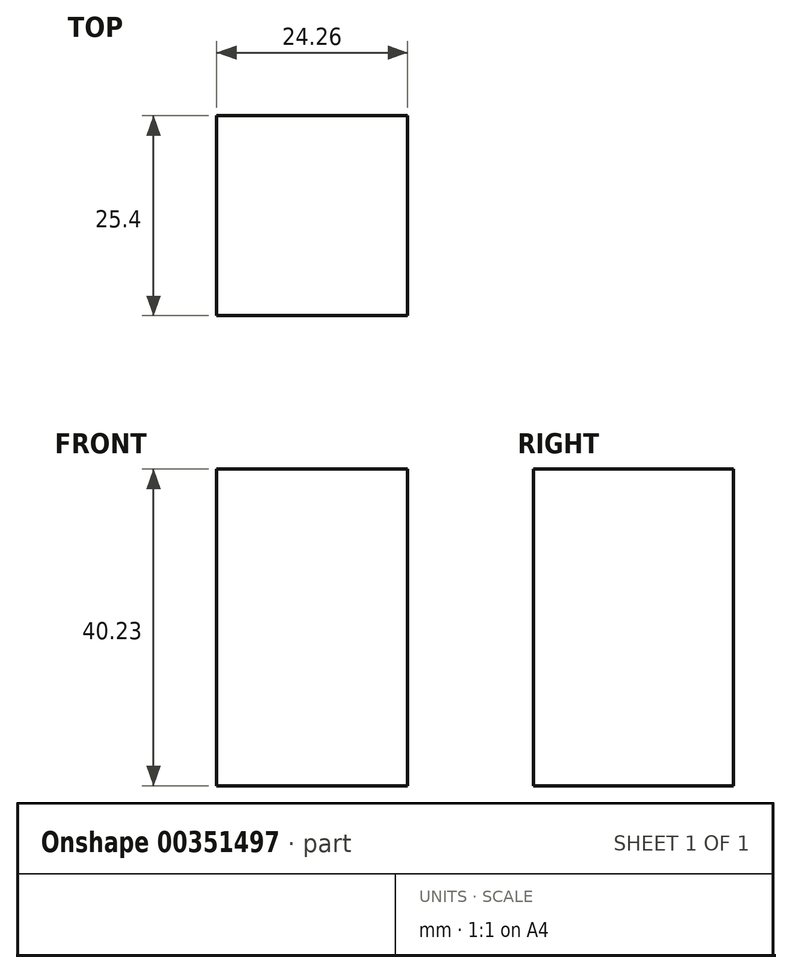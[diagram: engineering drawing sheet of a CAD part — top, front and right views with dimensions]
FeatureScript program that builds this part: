
annotation { "Feature Type Name" : "Feature", "Feature Type Description" : "" }
export const myFeature = defineFeature(function(context is Context, id is Id, definition is map)
    precondition{}
    {
        {
            var Q0;
            Q0=qCreatedBy(makeId("Front.planeOp"),FACE);
            var sketch = newSketch(context, id + "F0", { "sketchPlane" : qUnion([Q0])});
            skLineSegment(sketch, "E0.bottom", {"start": v(0, 0) * mm, "end": v(24.26, 0) * mm});
            skLineSegment(sketch, "E0.top", {"start": v(0, 40.23) * mm, "end": v(24.26, 40.23) * mm});
            skLineSegment(sketch, "E0.left", {"start": v(0, 0) * mm, "end": v(0, 40.23) * mm});
            skLineSegment(sketch, "E0.right", {"start": v(24.26, 0) * mm, "end": v(24.26, 40.23) * mm});
            skSolve(sketch);
        }
        {
            var Q0;
            Q0=makeQuery(id+"F0.imprint","IMPRINT",FACE,{"disambiguationData":[TD([[makeQuery(id+"F0.imprint","IMPRINT",EDGE,{"derivedFrom":sQuery(id+"F0.wireOp",EDGE,"E0.bottom")}),1.0]])]});
            extrude(context, id + "F1", {"entities" : qUnion([Q0]), "depth" : 25.4 * mm});
        }
    });
